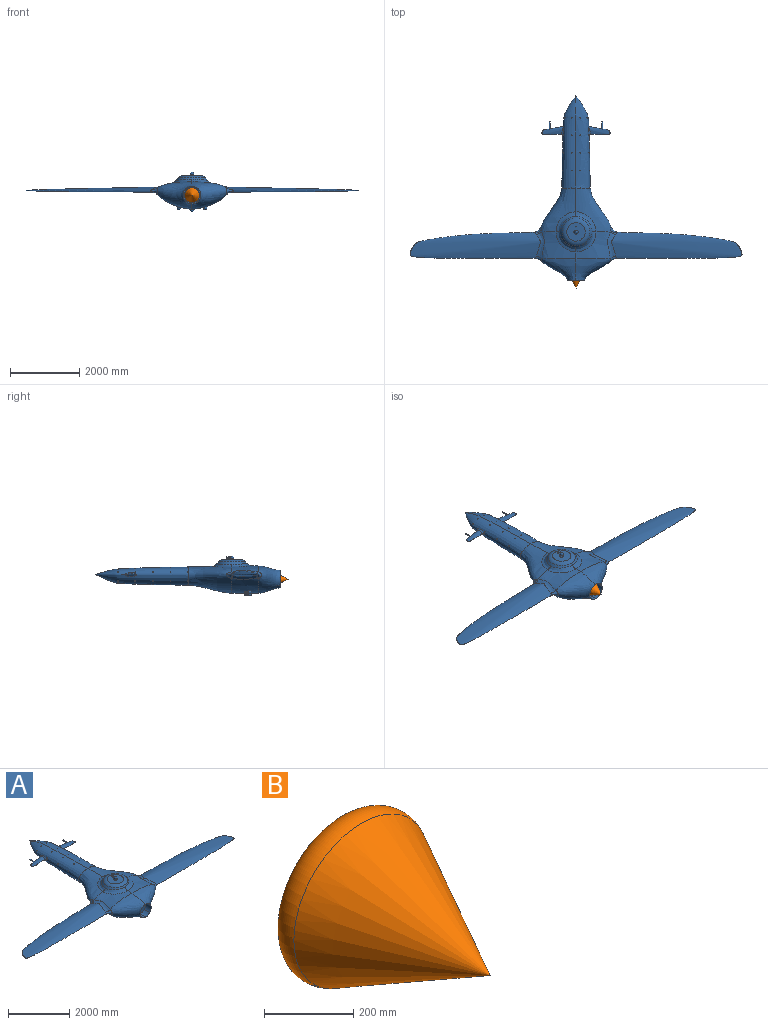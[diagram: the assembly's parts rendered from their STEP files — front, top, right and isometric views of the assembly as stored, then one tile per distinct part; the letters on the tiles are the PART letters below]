
ASSEMBLY  parts=2 mates=1
PART A: 187 faces, bbox 13589.5x5334x1155.7 mm
  f0: bspline ~1270x1036.44mm, area 1946422mm2, adj f1,f100,f101,f102,f103,f104,f105,f106
  f1: extruded ~995.01x762mm, area 844105.4mm2, adj f0,f2,f19,f64,f65,f82
  f2: sphere r=50.8mm, area 23373mm2, adj f1,f3,f7,f11,f15
  f3: cylinder r=12.7mm len=108.81mm, axis (0,1,0), area 8156.4mm2, adj f2,f4
  f4: torus R=6.35mm, axis (0,-1,0), area 651.3mm2, adj f3,f5
  f5: cylinder r=6.35mm len=110.15mm, axis (0,1,0), area 4270.5mm2, adj f4,f6
  f6: sphere r=50.8mm, area 141.2mm2, adj f5
  f7: cylinder r=12.7mm len=110.32mm, axis (0,1,0), area 8224.9mm2, adj f2,f8
  f8: torus R=6.35mm, axis (0,-1,0), area 651.3mm2, adj f7,f9
  f9: cylinder r=6.35mm len=111.23mm, axis (0,1,0), area 4302.2mm2, adj f8,f10
  f10: sphere r=50.8mm, area 143.8mm2, adj f9
  f11: cylinder r=12.7mm len=104.3mm, axis (0,1,0), area 8323mm2, adj f2,f12
  f12: torus R=6.35mm, axis (0,-1,0), area 651.3mm2, adj f11,f13
  f13: cylinder r=6.35mm len=105.08mm, axis (0,1,0), area 4192.6mm2, adj f12,f14
  f14: sphere r=50.8mm, area 134.4mm2, adj f13
  f15: cylinder r=12.7mm len=105.74mm, axis (0,1,0), area 8437.9mm2, adj f2,f16
  f16: torus R=6.35mm, axis (0,-1,0), area 651.3mm2, adj f15,f17
  f17: cylinder r=6.35mm len=107.99mm, axis (0,1,0), area 4208.2mm2, adj f16,f18
  f18: sphere r=50.8mm, area 136.5mm2, adj f17
  f19: bspline ~1036.35x785.31mm, area 1162564.2mm2, adj f1,f20,f24,f25,f61,f104
  f20: extruded ~254x186.24mm, area 53098mm2, adj f19,f21,f23,f24
  f21: plane 508x508mm, normal (0,-1,0), area 202688.6mm2, adj f20,f22,f23,f24
  f22: extruded ~426.72x254mm, area 149586.4mm2, adj f21,f23,f24,f25
  f23: extruded ~254x186.24mm, area 53097.8mm2, adj f20,f21,f22,f25
  f24: extruded ~426.72x254mm, area 149583.4mm2, adj f19,f20,f21,f22
  f25: bspline ~1036.35x785.31mm, area 1162564.2mm2, adj f19,f22,f23,f26,f34,f82
  f26: bspline ~219.13x194.66mm, area 35346.5mm2, adj f25,f27,f32,f33
  f27: bspline ~808.62x242.2mm, area 105497.7mm2, adj f26,f28,f32,f34
  f28: bspline ~184.63x142.86mm, area 9732.3mm2, adj f27,f29,f32,f106
  f29: bspline ~246.9x202.37mm, area 17719.8mm2, adj f28,f30,f32,f106
  f30: bspline ~241.81x196.61mm, area 19710.7mm2, adj f29,f31,f32,f106
  f31: bspline ~209.2x108.48mm, area 6366.9mm2, adj f30,f32,f33,f106
  f32: bspline ~6257.95x1180.14mm, area 4845672.1mm2, adj f26,f27,f28,f29,f30,f31,f33
  f33: bspline ~782.08x223.3mm, area 161757.5mm2, adj f26,f31,f32,f82
  f34: extruded ~985.62x762mm, area 505886.1mm2, adj f25,f27,f35,f104,f106
  f35: bspline ~618.36x584.03mm, area 126947.2mm2, adj f34,f36,f37,f38
  f36: bspline ~588.86x581.18mm, area 123308.8mm2, adj f35,f38,f105,f106
  f37: bspline ~618.36x584.85mm, area 126946.2mm2, adj f35,f38,f104,f105
  f38: sphere r=539.36mm, area 214399.3mm2, adj f35,f36,f37,f39,f105
  f39: torus R=266.46mm, axis (0,0,1), area 311016.1mm2, adj f38,f40
  f40: plane 532.92x532.92mm, normal (0,0,1), area 210384.4mm2, adj f39,f41
  f41: cylinder r=63.5mm len=127mm, axis (0,0,-1), area 86.1mm2, adj f40,f42
  f42: torus R=38.1mm, axis (0,0,1), area 13604.9mm2, adj f41,f43
  f43: plane 76.2x76.2mm, normal (0,0,1), area 257.2mm2, adj f42,f44
  f44: sphere r=50.8mm, area 25095mm2, adj f43,f45,f49,f53,f57
  f45: cylinder r=12.7mm len=106.26mm, axis (0,-1,0), area 8044.5mm2, adj f44,f46
  f46: torus R=6.35mm, axis (0,-1,0), area 651.3mm2, adj f45,f47
  f47: cylinder r=6.35mm len=108.31mm, axis (0,-1,0), area 4234.8mm2, adj f46,f48
  f48: sphere r=50.8mm, area 137.2mm2, adj f47
  f49: cylinder r=12.7mm len=106.26mm, axis (0,-1,0), area 8043.8mm2, adj f44,f50
  f50: torus R=6.35mm, axis (0,-1,0), area 651.3mm2, adj f49,f51
  f51: cylinder r=6.35mm len=108.31mm, axis (0,-1,0), area 4234.8mm2, adj f50,f52
  f52: sphere r=50.8mm, area 137.2mm2, adj f51
  f53: cylinder r=12.7mm len=107.75mm, axis (0,-1,0), area 8105.8mm2, adj f44,f54
  f54: torus R=6.35mm, axis (0,-1,0), area 651.3mm2, adj f53,f55
  f55: cylinder r=6.35mm len=109.39mm, axis (0,-1,0), area 4247.9mm2, adj f54,f56
  f56: sphere r=50.8mm, area 138.5mm2, adj f55
  f57: cylinder r=12.7mm len=107.75mm, axis (0,-1,0), area 8107.9mm2, adj f44,f58
  f58: torus R=6.35mm, axis (0,-1,0), area 651.3mm2, adj f57,f59
  f59: cylinder r=6.35mm len=109.39mm, axis (0,-1,0), area 4248.2mm2, adj f58,f60
  f60: sphere r=50.8mm, area 139.2mm2, adj f59
  f61: bspline ~219.13x194.66mm, area 35350.9mm2, adj f19,f62,f63,f64
  f62: bspline ~792.27x241.93mm, area 105491.6mm2, adj f61,f63,f103,f104
  f63: bspline ~6257.94x1180.14mm, area 4844157.5mm2, adj f61,f62,f64,f100,f101,f102,f103
  f64: bspline ~788.4x224mm, area 161750.4mm2, adj f1,f61,f63,f100
  f65: sphere r=50.8mm, area 24215.9mm2, adj f1,f66,f70,f74,f78,f82
  f66: cylinder r=12.7mm len=112.81mm, axis (0,-1,0), area 8336.5mm2, adj f65,f67
  f67: torus R=6.35mm, axis (0,-1,0), area 651.3mm2, adj f66,f68
  f68: cylinder r=6.35mm len=112.95mm, axis (0,-1,0), area 4353.5mm2, adj f67,f69
  f69: sphere r=50.8mm, area 146.5mm2, adj f68
  f70: cylinder r=12.7mm len=112.81mm, axis (0,-1,0), area 8337.9mm2, adj f65,f71
  f71: torus R=6.35mm, axis (0,-1,0), area 651.3mm2, adj f70,f72
  f72: cylinder r=6.35mm len=112.95mm, axis (0,-1,0), area 4353.5mm2, adj f71,f73
  f73: sphere r=50.8mm, area 146.5mm2, adj f72
  f74: cylinder r=12.7mm len=103.69mm, axis (0,-1,0), area 7933.1mm2, adj f65,f75
  f75: torus R=6.35mm, axis (0,-1,0), area 651.3mm2, adj f74,f76
  f76: cylinder r=6.35mm len=106.47mm, axis (0,-1,0), area 4166.3mm2, adj f75,f77
  f77: sphere r=50.8mm, area 132mm2, adj f76
  f78: cylinder r=12.7mm len=103.69mm, axis (0,-1,0), area 7932.9mm2, adj f65,f79
  f79: torus R=6.35mm, axis (0,-1,0), area 651.3mm2, adj f78,f80
  f80: cylinder r=6.35mm len=105.21mm, axis (0,-1,0), area 4164.8mm2, adj f79,f81
  f81: sphere r=50.8mm, area 131.6mm2, adj f80
  f82: extruded ~995.01x762mm, area 838596.6mm2, adj f1,f25,f33,f65,f83,f106
  f83: sphere r=50.8mm, area 23112.9mm2, adj f82,f84,f88,f92,f96
  f84: cylinder r=12.7mm len=107.49mm, axis (0,1,0), area 8096.8mm2, adj f83,f85
  f85: torus R=6.35mm, axis (0,-1,0), area 651.3mm2, adj f84,f86
  f86: cylinder r=6.35mm len=109.2mm, axis (0,1,0), area 4242.8mm2, adj f85,f87
  f87: sphere r=50.8mm, area 139.1mm2, adj f86
  f88: cylinder r=12.7mm len=112.33mm, axis (0,1,0), area 8316.2mm2, adj f83,f89
  f89: torus R=6.35mm, axis (0,-1,0), area 651.3mm2, adj f88,f90
  f90: cylinder r=6.35mm len=112.66mm, axis (0,1,0), area 4344.3mm2, adj f89,f91
  f91: sphere r=50.8mm, area 147.3mm2, adj f90
  f92: cylinder r=12.7mm len=107.56mm, axis (0,1,0), area 8583.2mm2, adj f83,f93
  f93: torus R=6.35mm, axis (0,-1,0), area 651.3mm2, adj f92,f94
  f94: cylinder r=6.35mm len=109.38mm, axis (0,1,0), area 4248.1mm2, adj f93,f95
  f95: sphere r=50.8mm, area 139.5mm2, adj f94
  f96: cylinder r=12.7mm len=102.97mm, axis (0,1,0), area 7903mm2, adj f83,f97
  f97: torus R=6.35mm, axis (0,-1,0), area 651.3mm2, adj f96,f98
  f98: cylinder r=6.35mm len=105.95mm, axis (0,1,0), area 4151.9mm2, adj f97,f99
  f99: sphere r=50.8mm, area 132.5mm2, adj f98
  f100: bspline ~211.13x111.05mm, area 6367.3mm2, adj f0,f63,f64,f101
  f101: bspline ~241.81x196.61mm, area 19710.9mm2, adj f0,f63,f100,f102
  f102: bspline ~246.9x202.36mm, area 17719.5mm2, adj f0,f63,f101,f103
  f103: bspline ~183.5x140.7mm, area 9732.5mm2, adj f0,f62,f63,f102
  f104: extruded ~985.62x762mm, area 505885mm2, adj f0,f19,f34,f37,f62
  f105: bspline ~588.86x581.18mm, area 123308.8mm2, adj f0,f36,f37,f38
  f106: bspline ~1270x1036.44mm, area 1946385.1mm2, adj f0,f28,f29,f30,f31,f34,f36,f82
  f107: cylinder r=12.7mm len=106.09mm, axis (0,0,1), area 7616mm2, adj f106,f108,f112,f114
  f108: cylinder r=12.7mm len=254mm, axis (-1,0,0), area 19047.2mm2, adj f107,f109,f111,f176
  f109: cylinder r=12.7mm len=254mm, axis (0,0,1), area 19047.2mm2, adj f108,f110,f112,f113
  f110: cylinder r=12.7mm len=254mm, axis (-1,0,0), area 20268.3mm2, adj f109,f111,f172,f173
  f111: cylinder r=12.7mm len=254mm, axis (0,0,1), area 19047.2mm2, adj f108,f110,f174,f175
  f112: cylinder r=12.7mm len=207.13mm, axis (-1,0,0), area 14835.5mm2, adj f106,f107,f109,f114
  f113: cylinder r=12.7mm len=268.02mm, axis (-1,0,0), area 20180.1mm2, adj f106,f109,f114,f172
  f114: bspline ~2667x526.8mm, area 2377148.2mm2, adj f106,f107,f112,f113,f115,f124,f133,f142
  f115: cylinder r=12.7mm len=237.09mm, axis (-1,0,0), area 17739.1mm2, adj f114,f116,f167
  f116: cylinder r=12.7mm len=254mm, axis (0,0,1), area 19047.2mm2, adj f115,f117,f123,f162
  f117: cylinder r=12.7mm len=254mm, axis (-1,0,0), area 19047.2mm2, adj f116,f118,f122,f166
  f118: cylinder r=12.7mm len=254mm, axis (0,0,1), area 19047.2mm2, adj f117,f119,f121,f123
  f119: cylinder r=12.7mm len=237.99mm, axis (-1,0,0), area 17808.6mm2, adj f118,f120,f177
  f120: cylinder r=12.7mm len=114.1mm, axis (0,0,1), area 8528.6mm2, adj f119,f123,f177
  f121: cylinder r=12.7mm len=165.14mm, axis (-1,0,0), area 11467.3mm2, adj f118,f122,f177
  f122: cylinder r=12.7mm len=75.14mm, axis (0,0,1), area 5419.9mm2, adj f117,f121,f177
  f123: cylinder r=12.7mm len=254mm, axis (-1,0,0), area 19047.2mm2, adj f116,f118,f120,f167
  f124: cylinder r=12.7mm len=258.69mm, axis (-1,0,0), area 19559.6mm2, adj f114,f125,f171
  f125: cylinder r=12.7mm len=254mm, axis (0,0,1), area 19047.2mm2, adj f124,f126,f132,f142
  f126: cylinder r=12.7mm len=254mm, axis (-1,0,0), area 19047.2mm2, adj f125,f127,f131,f170
  f127: cylinder r=12.7mm len=254mm, axis (0,0,1), area 19047.2mm2, adj f126,f128,f130,f132
  f128: cylinder r=12.7mm len=260.83mm, axis (-1,0,0), area 19725.9mm2, adj f127,f129,f177
  f129: cylinder r=12.7mm len=139.91mm, axis (0,0,1), area 10588mm2, adj f128,f132,f177
  f130: cylinder r=12.7mm len=203.55mm, axis (-1,0,0), area 14698.4mm2, adj f127,f131,f177
  f131: cylinder r=12.7mm len=100.52mm, axis (0,0,1), area 7445mm2, adj f126,f130,f177
  f132: cylinder r=12.7mm len=254mm, axis (-1,0,0), area 19047.2mm2, adj f125,f127,f129,f171
  f133: cylinder r=12.7mm len=107.69mm, axis (-1,0,0), area 6456.4mm2, adj f114,f134,f164
  f134: cylinder r=12.7mm len=254mm, axis (0,0,1), area 19047.2mm2, adj f133,f135,f141,f152
  f135: cylinder r=12.7mm len=254mm, axis (-1,0,0), area 19047.2mm2, adj f134,f136,f140,f164
  f136: cylinder r=12.7mm len=254mm, axis (0,0,1), area 19047.2mm2, adj f135,f137,f139,f141
  f137: cylinder r=12.7mm len=205.34mm, axis (-1,0,0), area 14748.2mm2, adj f136,f138,f177
  f138: cylinder r=12.7mm len=82.45mm, axis (0,0,1), area 6003mm2, adj f137,f141,f177
  f139: cylinder r=12.7mm len=107.71mm, axis (-1,0,0), area 6528.5mm2, adj f136,f140,f177
  f140: cylinder r=12.7mm len=39.21mm, axis (0,0,1), area 2553mm2, adj f135,f139,f177
  f141: cylinder r=12.7mm len=254mm, axis (-1,0,0), area 19047.2mm2, adj f134,f136,f138,f165
  f142: cylinder r=12.7mm len=202.09mm, axis (-1,0,0), area 14521.6mm2, adj f114,f125,f170
  f143: bspline ~295.03x108.05mm, area 31421mm2, adj f114,f144,f150,f151
  f144: bspline ~1015.9x358.87mm, area 200607.7mm2, adj f143,f145,f146,f150,f151
  f145: torus R=7.62mm, axis (0,1,0), area 1528.2mm2, adj f144,f146
  f146: cylinder r=12.7mm len=255.27mm, axis (0,-1,0), area 17606.1mm2, adj f144,f145,f147
  f147: torus R=6.35mm, axis (0,1,0), area 651.3mm2, adj f146,f148
  f148: cylinder r=6.35mm len=139.7mm, axis (0,-1,0), area 5573.8mm2, adj f147,f149
  f149: plane 12.7x12.7mm, normal (0,1,0), area 126.7mm2, adj f148
  f150: bspline ~56.61x55.15mm, area 1675mm2, adj f114,f143,f144,f151
  f151: bspline ~59.44x54.97mm, area 1492mm2, adj f114,f143,f144,f150
  f152: cylinder r=12.7mm len=205.31mm, axis (-1,0,0), area 14745.6mm2, adj f114,f134,f165
  f153: cylinder r=12.7mm len=189.58mm, axis (-1,0,0), area 13488mm2, adj f114,f154,f168
  f154: cylinder r=12.7mm len=254mm, axis (0,0,1), area 19047.2mm2, adj f153,f155,f161,f163
  f155: cylinder r=12.7mm len=254mm, axis (-1,0,0), area 19047.2mm2, adj f154,f156,f160,f168
  f156: cylinder r=12.7mm len=254mm, axis (0,0,1), area 19047.2mm2, adj f155,f157,f159,f161
  f157: cylinder r=12.7mm len=251.55mm, axis (-1,0,0), area 18992.9mm2, adj f156,f158,f177
  f158: cylinder r=12.7mm len=131.64mm, axis (0,0,1), area 9928.3mm2, adj f157,f161,f177
  f159: cylinder r=12.7mm len=190.92mm, axis (-1,0,0), area 13656.4mm2, adj f156,f160,f177
  f160: cylinder r=12.7mm len=92.76mm, axis (0,0,1), area 6825.7mm2, adj f155,f159,f177
  f161: cylinder r=12.7mm len=254mm, axis (-1,0,0), area 19047.2mm2, adj f154,f156,f158,f169
  f162: cylinder r=12.7mm len=164.58mm, axis (-1,0,0), area 11356.2mm2, adj f114,f116,f166
  f163: cylinder r=12.7mm len=249.54mm, axis (-1,0,0), area 18836mm2, adj f114,f154,f169
  f164: cylinder r=12.7mm len=48.26mm, axis (0,0,1), area 3275.4mm2, adj f114,f133,f135
  f165: cylinder r=12.7mm len=87.14mm, axis (0,0,1), area 6446.9mm2, adj f114,f141,f152
  f166: cylinder r=12.7mm len=82.06mm, axis (0,0,1), area 5971.9mm2, adj f114,f117,f162
  f167: cylinder r=12.7mm len=116.5mm, axis (0,0,1), area 8789.2mm2, adj f114,f115,f123
  f168: cylinder r=12.7mm len=98.91mm, axis (0,0,1), area 7316.3mm2, adj f114,f153,f155
  f169: cylinder r=12.7mm len=133.64mm, axis (0,0,1), area 10157mm2, adj f114,f161,f163
  f170: cylinder r=12.7mm len=106.77mm, axis (0,0,1), area 7943.9mm2, adj f114,f126,f142
  f171: cylinder r=12.7mm len=142.71mm, axis (0,0,1), area 10881.3mm2, adj f114,f124,f132
  f172: cylinder r=12.7mm len=144.03mm, axis (0,0,1), area 10744mm2, adj f106,f110,f113,f114
  f173: cylinder r=12.7mm len=144.03mm, axis (0,0,1), area 10744mm2, adj f0,f110,f174,f177
  f174: cylinder r=12.7mm len=268.02mm, axis (-1,0,0), area 20180.1mm2, adj f0,f111,f173,f177
  f175: cylinder r=12.7mm len=207.13mm, axis (-1,0,0), area 14904.7mm2, adj f0,f111,f176,f177
  f176: cylinder r=12.7mm len=106.09mm, axis (0,0,1), area 7616mm2, adj f0,f108,f175,f177
  f177: bspline ~2667x526.8mm, area 2380624.8mm2, adj f0,f114,f119,f120,f121,f122,f128,f129
  f178: bspline ~293.49x107.99mm, area 31238.3mm2, adj f177,f179,f185,f186
  f179: bspline ~1015.9x358.87mm, area 199700.6mm2, adj f178,f180,f181,f185,f186
  f180: torus R=7.62mm, axis (0,1,0), area 0mm2, adj f179,f181
  f181: cylinder r=12.7mm len=255.27mm, axis (0,-1,0), area 17599.9mm2, adj f179,f180,f182
  f182: torus R=6.35mm, axis (0,1,0), area 651.3mm2, adj f181,f183
  f183: cylinder r=6.35mm len=139.7mm, axis (0,-1,0), area 5573.8mm2, adj f182,f184
  f184: plane 12.7x12.7mm, normal (0,1,0), area 126.7mm2, adj f183
  f185: bspline ~59.53x55.14mm, area 1495.2mm2, adj f177,f178,f179,f186
  f186: bspline ~56.95x55.34mm, area 1698.5mm2, adj f177,f178,f179,f185
PART B: 3 faces, bbox 477.7x482.6x477.7 mm
  f0: plane 339.71x339.71mm, normal (0,1,0), area 90639.1mm2, adj f2
  f1: cone r=254mm half-angle=27.8deg, axis (0,1,0), area 311251.6mm2, adj f2
  f2: torus R=169.86mm, axis (0,-1,0), area 135195mm2, adj f0,f1
PLACE A t=(1095.01,6021.71,-1067.82)mm
PLACE B t=(1095.01,6224.91,-1067.84)mm
MATE fastened B.f1 <-> A.f21  axis (0,1,0) through (1095.01,941.71,-1204.15)mm
